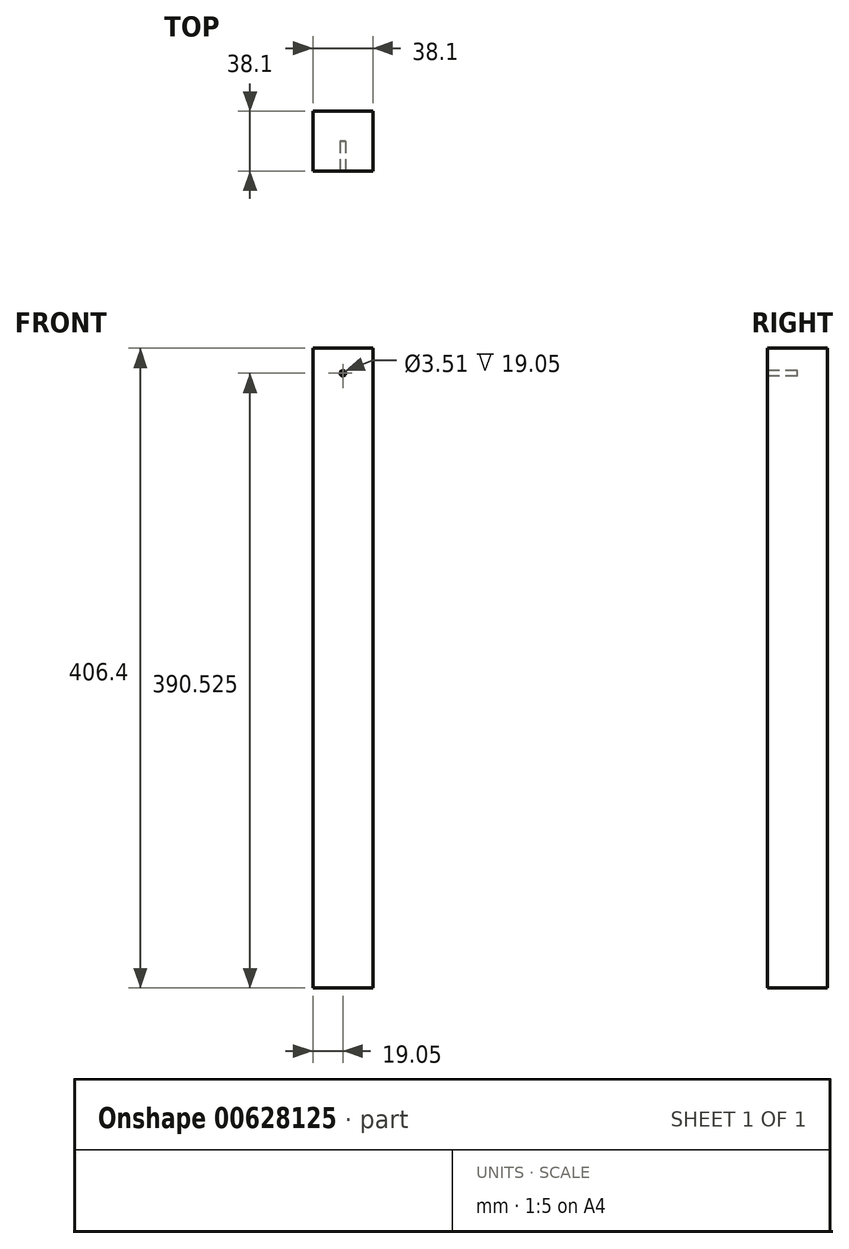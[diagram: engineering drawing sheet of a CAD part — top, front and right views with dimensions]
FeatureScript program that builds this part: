
annotation { "Feature Type Name" : "Feature", "Feature Type Description" : "" }
export const myFeature = defineFeature(function(context is Context, id is Id, definition is map)
    precondition{}
    {
        {
            var Q0;
            Q0=qCreatedBy(makeId("Top.planeOp"),FACE);
            var sketch = newSketch(context, id + "F0", { "sketchPlane" : qUnion([Q0])});
            skLineSegment(sketch, "E0.bottom", {"start": v(19.05, 19.05) * mm, "end": v(-19.05, 19.05) * mm});
            skLineSegment(sketch, "E0.top", {"start": v(19.05, -19.05) * mm, "end": v(-19.05, -19.05) * mm});
            skLineSegment(sketch, "E0.left", {"start": v(19.05, 19.05) * mm, "end": v(19.05, -19.05) * mm});
            skLineSegment(sketch, "E0.right", {"start": v(-19.05, 19.05) * mm, "end": v(-19.05, -19.05) * mm});
            skPoint(sketch, "E0.middle", {"position": v(0, 0) * mm});
            skSolve(sketch);
        }
        {
            var Q0;
            Q0=makeQuery(id+"F0.imprint","IMPRINT",FACE,{"disambiguationData":[TD([[makeQuery(id+"F0.imprint","IMPRINT",EDGE,{"derivedFrom":sQuery(id+"F0.wireOp",EDGE,"E0.bottom")}),1.0]])]});
            extrude(context, id + "F1", {"entities" : qUnion([Q0]), "depth" : 406.4 * mm, "offsetDistance" : 25.4 * mm});
        }
        {
            var Q0;
            Q0=makeQuery(id+"F1.opExtrude","SWEPT_FACE",FACE,{"disambiguationData":[OSD([sQuery(id+"F0.wireOp",EDGE,"E0.top")])]});
            var sketch = newSketch(context, id + "F2", { "sketchPlane" : qUnion([Q0])});
            skLineSegment(sketch, "E1", {"start": v(0, 406.4) * mm, "end": v(0, 390.53) * mm, "construction": true});
            skPoint(sketch, "E1.endSnap0", {"position": v(0, 406.4) * mm});
            skCircle(sketch, "E2", {"center": v(0, 390.53) * mm, "radius": 1.75 * mm});
            skSolve(sketch);
        }
        {
            var Q0;
            Q0=makeQuery(id+"F2.imprint","IMPRINT",FACE,{"disambiguationData":[TD([[makeQuery(id+"F2.imprint","IMPRINT",EDGE,{"derivedFrom":sQuery(id+"F2.wireOp",EDGE,"E2")}),1.0]])]});
            extrude(context, id + "F3", {"entities" : qUnion([Q0]), "operationType" : NewBodyOperationType.REMOVE, "oppositeDirection" : true, "depth" : 19.05 * mm, "offsetDistance" : 25.4 * mm});
        }
    });
